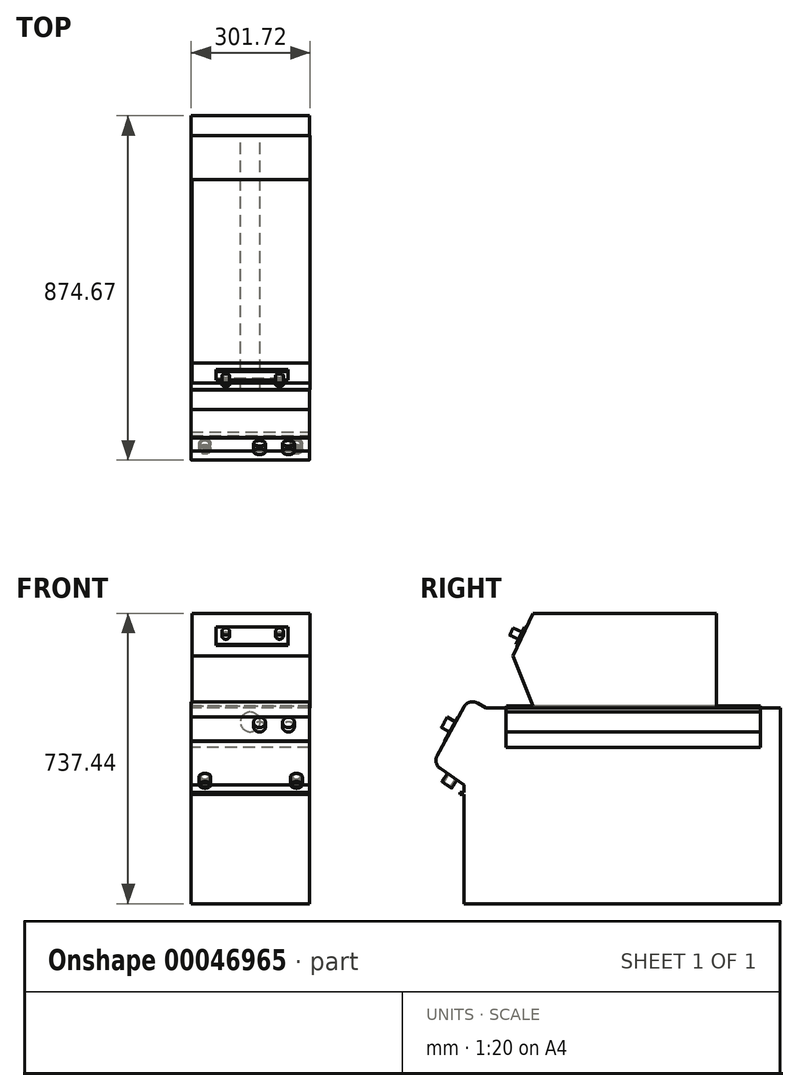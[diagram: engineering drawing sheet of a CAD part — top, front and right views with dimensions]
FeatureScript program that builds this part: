
annotation { "Feature Type Name" : "Feature", "Feature Type Description" : "" }
export const myFeature = defineFeature(function(context is Context, id is Id, definition is map)
    precondition{}
    {
        {
            var Q0;
            Q0=qCreatedBy(makeId("Right.planeOp"),FACE);
            var sketch = newSketch(context, id + "F0", { "sketchPlane" : qUnion([Q0])});
            skLineSegment(sketch, "E0.rect.top", {"start": v(-373.5, -248.5) * mm, "end": v(373.5, -248.5) * mm});
            skLineSegment(sketch, "E0.rect.left", {"start": v(-373.5, 248.5) * mm, "end": v(-373.5, -248.5) * mm});
            skLineSegment(sketch, "E0.rect.right", {"start": v(373.5, 248.5) * mm, "end": v(373.5, -248.5) * mm});
            skPoint(sketch, "E0.rect.middle", {"position": v(0, 0) * mm});
            skLineSegment(sketch, "E1", {"start": v(-323.5, 248.5) * mm, "end": v(-323.5, 148.5) * mm});
            skLineSegment(sketch, "E2", {"start": v(-323.5, 148.5) * mm, "end": v(323.5, 148.5) * mm});
            skLineSegment(sketch, "E3", {"start": v(323.5, 148.5) * mm, "end": v(323.5, 248.5) * mm});
            skLineSegment(sketch, "E4", {"start": v(-373.5, 248.5) * mm, "end": v(-323.5, 248.5) * mm});
            skLineSegment(sketch, "E5", {"start": v(323.5, 248.5) * mm, "end": v(373.5, 248.5) * mm});
            skSolve(sketch);
        }
        {
            var Q0;
            Q0=qSketchRegion(id+"F0",true);
            extrude(context, id + "F1", {"entities" : qUnion([Q0]), "depth" : 300 * mm});
        }
        {
            var Q0;
            Q0=makeQuery(id+"F1.opExtrude","SWEPT_FACE",FACE,{"disambiguationData":[OSD([sQuery(id+"F0.wireOp",EDGE,"E3")])]});
            var sketch = newSketch(context, id + "F2", { "sketchPlane" : qUnion([Q0])});
            skLineSegment(sketch, "E6", {"start": v(0, 248.5) * mm, "end": v(300, 148.5) * mm, "construction": true});
            skLineSegment(sketch, "E7", {"start": v(300, 248.5) * mm, "end": v(0, 148.5) * mm, "construction": true});
            skCircle(sketch, "E8", {"center": v(150, 213.5) * mm, "radius": 25 * mm});
            skPoint(sketch, "E8.centerSnap0", {"position": v(150, 198.5) * mm});
            skSolve(sketch);
        }
        {
            var Q0;
            Q0=qSketchRegion(id+"F2",true);
            var Q1;
            Q1=makeQuery(id+"F1.opExtrude","SWEPT_FACE",FACE,{"disambiguationData":[OSD([sQuery(id+"F0.wireOp",EDGE,"E1")])]});
            extrude(context, id + "F3", {"entities" : qUnion([Q0]), "endBound" : BoundingType.UP_TO_SURFACE, "endBoundEntityFace" : qUnion([Q1]), "depth" : 25 * mm});
        }
        {
            var Q0;
            Q0=makeQuery(id+"F1.opExtrude","CAP_FACE",FACE,{"disambiguationData":[OSD([sQuery(id+"F0.wireOp",EDGE,"E0.rect.top"),sQuery(id+"F0.wireOp",EDGE,"E0.rect.left"),sQuery(id+"F0.wireOp",EDGE,"E0.rect.right"),sQuery(id+"F0.wireOp",EDGE,"E1"),sQuery(id+"F0.wireOp",EDGE,"E2"),sQuery(id+"F0.wireOp",EDGE,"E3"),sQuery(id+"F0.wireOp",EDGE,"E4"),sQuery(id+"F0.wireOp",EDGE,"E5")])],"isStart":false});
            var sketch = newSketch(context, id + "F4", { "sketchPlane" : qUnion([Q0])});
            skLineSegment(sketch, "E9", {"start": v(-373.5, 248.5) * mm, "end": v(-417.97, 273.97) * mm});
            skLineSegment(sketch, "E10", {"start": v(-417.97, 273.97) * mm, "end": v(-509.02, 107.56) * mm});
            skLineSegment(sketch, "E11", {"start": v(-509.02, 107.56) * mm, "end": v(-429.45, 53.73) * mm});
            skLineSegment(sketch, "E12", {"start": v(-429.45, 53.73) * mm, "end": v(-429.45, -248.5) * mm});
            skLineSegment(sketch, "E13", {"start": v(-429.45, -248.5) * mm, "end": v(-373.5, -248.5) * mm});
            skSolve(sketch);
        }
        {
            var Q0;
            Q0=makeQuery(id+"F4.imprint","IMPRINT",FACE,{"disambiguationData":[TD([[makeQuery(id+"F4.imprint","IMPRINT",EDGE,{"derivedFrom":sQuery(id+"F4.wireOp",EDGE,"E9")}),1.0]])]});
            extrude(context, id + "F5", {"entities" : qUnion([Q0]), "operationType" : NewBodyOperationType.ADD, "oppositeDirection" : true, "depth" : 300 * mm});
        }
        {
            var Q0;
            Q0=makeQuery(id+"F5.opExtrude","SWEPT_EDGE",EDGE,{"disambiguationData":[OSD([sQuery(id+"F4.wireOp",EDGE,"E9"),sQuery(id+"F4.wireOp",EDGE,"E10")])]});
            fillet(context, id + "F6", {"entities" : qUnion([Q0]), "radius" : 25 * mm, "tangentPropagation" : true, "allowEdgeOverflow" : false});
        }
        {
            var Q0;
            Q0=makeQuery(id+"F5.opExtrude","SWEPT_EDGE",EDGE,{"disambiguationData":[OSD([sQuery(id+"F4.wireOp",EDGE,"E10"),sQuery(id+"F4.wireOp",EDGE,"E11")])]});
            fillet(context, id + "F7", {"entities" : qUnion([Q0]), "radius" : 25 * mm, "tangentPropagation" : true, "allowEdgeOverflow" : false});
        }
        {
            var Q0;
            Q0=makeQuery(id+"F5.opExtrude","SWEPT_FACE",FACE,{"disambiguationData":[OSD([sQuery(id+"F4.wireOp",EDGE,"E10")])]});
            var sketch = newSketch(context, id + "F8", { "sketchPlane" : qUnion([Q0])});
            skCircle(sketch, "E14", {"center": v(247, -44.1) * mm, "radius": 15 * mm});
            skCircle(sketch, "E15", {"center": v(173.6, -44.1) * mm, "radius": 15 * mm});
            skLineSegment(sketch, "E16.bottom", {"start": v(0, -15) * mm, "end": v(300, -15) * mm});
            skLineSegment(sketch, "E16.top", {"start": v(0, -85.4) * mm, "end": v(300, -85.4) * mm});
            skLineSegment(sketch, "E16.left", {"start": v(0, -15) * mm, "end": v(0, -85.4) * mm});
            skLineSegment(sketch, "E16.right", {"start": v(300, -15) * mm, "end": v(300, -85.4) * mm});
            skLineSegment(sketch, "E17", {"start": v(173.6, -44.1) * mm, "end": v(247, -44.1) * mm, "construction": true});
            skSolve(sketch);
        }
        {
            var Q0;
            Q0=makeQuery(id+"F8.imprint","IMPRINT",FACE,{"disambiguationData":[TD([[makeQuery(id+"F8.imprint","IMPRINT",EDGE,{"derivedFrom":sQuery(id+"F8.wireOp",EDGE,"E14")}),-1.0]])]});
            extrude(context, id + "F9", {"entities" : qUnion([Q0]), "depth" : 1 * mm});
        }
        {
            var Q0;
            Q0=makeQuery(id+"F8.imprint","IMPRINT",FACE,{"disambiguationData":[TD([[makeQuery(id+"F8.imprint","IMPRINT",EDGE,{"derivedFrom":sQuery(id+"F8.wireOp",EDGE,"E15")}),1.0]])]});
            extrude(context, id + "F10", {"entities" : qUnion([Q0]), "depth" : 25 * mm});
        }
        {
            var Q0;
            Q0=makeQuery(id+"F8.imprint","IMPRINT",FACE,{"disambiguationData":[TD([[makeQuery(id+"F8.imprint","IMPRINT",EDGE,{"derivedFrom":sQuery(id+"F8.wireOp",EDGE,"E14")}),1.0]])]});
            extrude(context, id + "F11", {"entities" : qUnion([Q0]), "depth" : 25 * mm});
        }
        {
            var Q0;
            Q0=makeQuery(id+"F5.opExtrude","SWEPT_FACE",FACE,{"disambiguationData":[OSD([sQuery(id+"F4.wireOp",EDGE,"E11")])]});
            var sketch = newSketch(context, id + "F12", { "sketchPlane" : qUnion([Q0])});
            skCircle(sketch, "E18", {"center": v(34.76, 422.44) * mm, "radius": 15 * mm});
            skPoint(sketch, "E18.centerSnap0", {"position": v(0, 422.44) * mm});
            skCircle(sketch, "E19", {"center": v(267.24, 422.44) * mm, "radius": 15 * mm});
            skCircle(sketch, "E20", {"center": v(34.76, 422.44) * mm, "radius": 10 * mm});
            skCircle(sketch, "E21", {"center": v(267.24, 422.44) * mm, "radius": 10 * mm});
            skSolve(sketch);
        }
        {
            var Q0;
            Q0=qSketchRegion(id+"F12",true);
            extrude(context, id + "F13", {"entities" : qUnion([Q0]), "depth" : 25 * mm});
        }
        {
            var Q0;
            Q0=makeQuery(id+"F5.opExtrude","SWEPT_FACE",FACE,{"disambiguationData":[OSD([sQuery(id+"F4.wireOp",EDGE,"E12")])]});
            var sketch = newSketch(context, id + "F14", { "sketchPlane" : qUnion([Q0])});
            skLineSegment(sketch, "E22.bottom", {"start": v(0, 41.73) * mm, "end": v(300, 41.73) * mm});
            skLineSegment(sketch, "E22.top", {"start": v(0, -238.27) * mm, "end": v(300, -238.27) * mm});
            skLineSegment(sketch, "E22.left", {"start": v(0, 41.73) * mm, "end": v(0, -238.27) * mm});
            skLineSegment(sketch, "E22.right", {"start": v(300, 41.73) * mm, "end": v(300, -238.27) * mm});
            skLineSegment(sketch, "E23.bottom", {"start": v(0, 34.33) * mm, "end": v(300, 34.33) * mm});
            skLineSegment(sketch, "E23.top", {"start": v(0, 29.42) * mm, "end": v(300, 29.42) * mm});
            skLineSegment(sketch, "E23.left", {"start": v(0, 34.33) * mm, "end": v(0, 29.42) * mm});
            skLineSegment(sketch, "E23.right", {"start": v(300, 34.33) * mm, "end": v(300, 29.42) * mm});
            skLineSegment(sketch, "E24", {"start": v(0, -97.39) * mm, "end": v(300, -97.39) * mm, "construction": true});
            skLineSegment(sketch, "E25.MirrorCS", {"start": v(300, -229.1) * mm, "end": v(300, -224.2) * mm});
            skLineSegment(sketch, "E26.MirrorCS", {"start": v(0, -229.1) * mm, "end": v(0, -224.2) * mm});
            skLineSegment(sketch, "E27.MirrorCS", {"start": v(0, -229.1) * mm, "end": v(300, -229.1) * mm});
            skLineSegment(sketch, "E28.MirrorCS", {"start": v(0, -224.2) * mm, "end": v(300, -224.2) * mm});
            skLineSegment(sketch, "E29", {"start": v(0, 24.35) * mm, "end": v(300, 24.35) * mm, "construction": true});
            skLineSegment(sketch, "E30.MirrorCS", {"start": v(0, 14.36) * mm, "end": v(0, 19.27) * mm});
            skLineSegment(sketch, "E31.MirrorCS", {"start": v(300, 14.36) * mm, "end": v(300, 19.27) * mm});
            skLineSegment(sketch, "E32.MirrorCS", {"start": v(0, 14.36) * mm, "end": v(300, 14.36) * mm});
            skLineSegment(sketch, "E33.MirrorCS", {"start": v(0, 19.27) * mm, "end": v(300, 19.27) * mm});
            skLineSegment(sketch, "E34.MirrorCS", {"start": v(0, 6.97) * mm, "end": v(300, 6.97) * mm, "construction": true});
            skLineSegment(sketch, "E35.MirrorCS", {"start": v(0, -20.4) * mm, "end": v(0, -15.49) * mm});
            skLineSegment(sketch, "E36.MirrorCS", {"start": v(300, -20.4) * mm, "end": v(300, -15.49) * mm});
            skLineSegment(sketch, "E37.MirrorCS", {"start": v(0, -0.43) * mm, "end": v(0, -5.34) * mm});
            skLineSegment(sketch, "E38.MirrorCS", {"start": v(300, -0.43) * mm, "end": v(300, -5.34) * mm});
            skLineSegment(sketch, "E39.MirrorCS", {"start": v(0, -20.4) * mm, "end": v(300, -20.4) * mm});
            skLineSegment(sketch, "E40.MirrorCS", {"start": v(0, -15.49) * mm, "end": v(300, -15.49) * mm});
            skLineSegment(sketch, "E41.MirrorCS", {"start": v(0, -27.8) * mm, "end": v(300, -27.8) * mm, "construction": true});
            skLineSegment(sketch, "E42.MirrorCS", {"start": v(0, -5.34) * mm, "end": v(300, -5.34) * mm});
            skLineSegment(sketch, "E43.MirrorCS", {"start": v(0, -0.43) * mm, "end": v(300, -0.43) * mm});
            skLineSegment(sketch, "E44.MirrorCS", {"start": v(0, -10.41) * mm, "end": v(300, -10.41) * mm, "construction": true});
            skLineSegment(sketch, "E45.MirrorCS", {"start": v(300, -89.92) * mm, "end": v(300, -85) * mm});
            skLineSegment(sketch, "E46.MirrorCS", {"start": v(300, -35.2) * mm, "end": v(300, -40.1) * mm});
            skLineSegment(sketch, "E47.MirrorCS", {"start": v(0, -35.2) * mm, "end": v(0, -40.1) * mm});
            skLineSegment(sketch, "E48.MirrorCS", {"start": v(300, -69.95) * mm, "end": v(300, -74.86) * mm});
            skLineSegment(sketch, "E49.MirrorCS", {"start": v(0, -69.95) * mm, "end": v(0, -74.86) * mm});
            skLineSegment(sketch, "E50.MirrorCS", {"start": v(300, -55.16) * mm, "end": v(300, -50.25) * mm});
            skLineSegment(sketch, "E51.MirrorCS", {"start": v(0, -55.16) * mm, "end": v(0, -50.25) * mm});
            skLineSegment(sketch, "E52.MirrorCS", {"start": v(0, -89.92) * mm, "end": v(0, -85) * mm});
            skLineSegment(sketch, "E53.MirrorCS", {"start": v(0, -55.16) * mm, "end": v(300, -55.16) * mm});
            skLineSegment(sketch, "E54.MirrorCS", {"start": v(0, -69.95) * mm, "end": v(300, -69.95) * mm});
            skLineSegment(sketch, "E55.MirrorCS", {"start": v(0, -50.25) * mm, "end": v(300, -50.25) * mm});
            skLineSegment(sketch, "E56.MirrorCS", {"start": v(0, -97.31) * mm, "end": v(300, -97.31) * mm, "construction": true});
            skLineSegment(sketch, "E57.MirrorCS", {"start": v(0, -79.93) * mm, "end": v(300, -79.93) * mm, "construction": true});
            skLineSegment(sketch, "E58.MirrorCS", {"start": v(0, -62.55) * mm, "end": v(300, -62.55) * mm, "construction": true});
            skLineSegment(sketch, "E59.MirrorCS", {"start": v(0, -89.92) * mm, "end": v(300, -89.92) * mm});
            skLineSegment(sketch, "E60.MirrorCS", {"start": v(0, -40.1) * mm, "end": v(300, -40.1) * mm});
            skLineSegment(sketch, "E61.MirrorCS", {"start": v(0, -45.17) * mm, "end": v(300, -45.17) * mm, "construction": true});
            skLineSegment(sketch, "E62.MirrorCS", {"start": v(0, -74.86) * mm, "end": v(300, -74.86) * mm});
            skLineSegment(sketch, "E63.MirrorCS", {"start": v(0, -35.2) * mm, "end": v(300, -35.2) * mm});
            skLineSegment(sketch, "E64.MirrorCS", {"start": v(0, -85) * mm, "end": v(300, -85) * mm});
            skLineSegment(sketch, "E65.MirrorCS", {"start": v(300, -174.38) * mm, "end": v(300, -179.29) * mm});
            skLineSegment(sketch, "E66.MirrorCS", {"start": v(0, -139.62) * mm, "end": v(0, -144.53) * mm});
            skLineSegment(sketch, "E67.MirrorCS", {"start": v(0, -174.38) * mm, "end": v(0, -179.29) * mm});
            skLineSegment(sketch, "E68.MirrorCS", {"start": v(0, -124.82) * mm, "end": v(0, -119.91) * mm});
            skLineSegment(sketch, "E69.MirrorCS", {"start": v(0, -194.34) * mm, "end": v(0, -189.43) * mm});
            skLineSegment(sketch, "E70.MirrorCS", {"start": v(300, -139.62) * mm, "end": v(300, -144.53) * mm});
            skLineSegment(sketch, "E71.MirrorCS", {"start": v(300, -124.82) * mm, "end": v(300, -119.91) * mm});
            skLineSegment(sketch, "E72.MirrorCS", {"start": v(300, -104.86) * mm, "end": v(300, -109.77) * mm});
            skLineSegment(sketch, "E73.MirrorCS", {"start": v(0, -104.86) * mm, "end": v(0, -109.77) * mm});
            skLineSegment(sketch, "E74.MirrorCS", {"start": v(300, -209.14) * mm, "end": v(300, -214.05) * mm});
            skLineSegment(sketch, "E75.MirrorCS", {"start": v(300, -194.34) * mm, "end": v(300, -189.43) * mm});
            skLineSegment(sketch, "E76.MirrorCS", {"start": v(0, -159.58) * mm, "end": v(0, -154.67) * mm});
            skLineSegment(sketch, "E77.MirrorCS", {"start": v(0, -209.14) * mm, "end": v(0, -214.05) * mm});
            skLineSegment(sketch, "E78.MirrorCS", {"start": v(300, -159.58) * mm, "end": v(300, -154.67) * mm});
            skLineSegment(sketch, "E79.MirrorCS", {"start": v(0, -194.34) * mm, "end": v(300, -194.34) * mm});
            skLineSegment(sketch, "E80.MirrorCS", {"start": v(0, -104.86) * mm, "end": v(300, -104.86) * mm});
            skLineSegment(sketch, "E81.MirrorCS", {"start": v(0, -109.77) * mm, "end": v(300, -109.77) * mm});
            skLineSegment(sketch, "E82.MirrorCS", {"start": v(0, -209.14) * mm, "end": v(300, -209.14) * mm});
            skLineSegment(sketch, "E83.MirrorCS", {"start": v(0, -149.6) * mm, "end": v(300, -149.6) * mm, "construction": true});
            skLineSegment(sketch, "E84.MirrorCS", {"start": v(0, -189.43) * mm, "end": v(300, -189.43) * mm});
            skLineSegment(sketch, "E85.MirrorCS", {"start": v(0, -132.22) * mm, "end": v(300, -132.22) * mm, "construction": true});
            skLineSegment(sketch, "E86.MirrorCS", {"start": v(0, -144.53) * mm, "end": v(300, -144.53) * mm});
            skLineSegment(sketch, "E87.MirrorCS", {"start": v(0, -174.38) * mm, "end": v(300, -174.38) * mm});
            skLineSegment(sketch, "E88.MirrorCS", {"start": v(0, -214.05) * mm, "end": v(300, -214.05) * mm});
            skLineSegment(sketch, "E89.MirrorCS", {"start": v(0, -154.67) * mm, "end": v(300, -154.67) * mm});
            skLineSegment(sketch, "E90.MirrorCS", {"start": v(0, -184.36) * mm, "end": v(300, -184.36) * mm, "construction": true});
            skLineSegment(sketch, "E91.MirrorCS", {"start": v(0, -166.98) * mm, "end": v(300, -166.98) * mm, "construction": true});
            skLineSegment(sketch, "E92.MirrorCS", {"start": v(0, -114.84) * mm, "end": v(300, -114.84) * mm, "construction": true});
            skLineSegment(sketch, "E93.MirrorCS", {"start": v(0, -236.5) * mm, "end": v(300, -236.5) * mm});
            skLineSegment(sketch, "E94.MirrorCS", {"start": v(0, -119.91) * mm, "end": v(300, -119.91) * mm});
            skLineSegment(sketch, "E95.MirrorCS", {"start": v(0, -139.62) * mm, "end": v(300, -139.62) * mm});
            skLineSegment(sketch, "E96.MirrorCS", {"start": v(0, -219.12) * mm, "end": v(300, -219.12) * mm, "construction": true});
            skLineSegment(sketch, "E97.MirrorCS", {"start": v(0, -124.82) * mm, "end": v(300, -124.82) * mm});
            skLineSegment(sketch, "E98.MirrorCS", {"start": v(0, -159.58) * mm, "end": v(300, -159.58) * mm});
            skLineSegment(sketch, "E99.MirrorCS", {"start": v(0, -97.46) * mm, "end": v(300, -97.46) * mm, "construction": true});
            skLineSegment(sketch, "E100.MirrorCS", {"start": v(0, -179.29) * mm, "end": v(300, -179.29) * mm});
            skLineSegment(sketch, "E101.MirrorCS", {"start": v(0, -201.74) * mm, "end": v(300, -201.74) * mm, "construction": true});
            skSolve(sketch);
        }
        {
            var Q0;
            Q0=makeQuery(id+"F14.imprint","IMPRINT",FACE,{"disambiguationData":[TD([[makeQuery(id+"F14.imprint","IMPRINT",EDGE,{"derivedFrom":sQuery(id+"F14.wireOp",EDGE,"E23.bottom")}),-1.0]])]});
            var Q1;
            Q1=makeQuery(id+"F14.imprint","IMPRINT",FACE,{"disambiguationData":[TD([[makeQuery(id+"F14.imprint","IMPRINT",EDGE,{"derivedFrom":sQuery(id+"F14.wireOp",EDGE,"E30.MirrorCS")}),1.0]])]});
            var Q2;
            Q2=makeQuery(id+"F14.imprint","IMPRINT",FACE,{"disambiguationData":[TD([[makeQuery(id+"F14.imprint","IMPRINT",EDGE,{"derivedFrom":sQuery(id+"F14.wireOp",EDGE,"E37.MirrorCS")}),1.0]])]});
            var Q3;
            Q3=makeQuery(id+"F14.imprint","IMPRINT",FACE,{"disambiguationData":[TD([[makeQuery(id+"F14.imprint","IMPRINT",EDGE,{"derivedFrom":sQuery(id+"F14.wireOp",EDGE,"E35.MirrorCS")}),1.0]])]});
            var Q4;
            Q4=makeQuery(id+"F14.imprint","IMPRINT",FACE,{"disambiguationData":[TD([[makeQuery(id+"F14.imprint","IMPRINT",EDGE,{"derivedFrom":sQuery(id+"F14.wireOp",EDGE,"E46.MirrorCS")}),-1.0]])]});
            var Q5;
            Q5=makeQuery(id+"F14.imprint","IMPRINT",FACE,{"disambiguationData":[TD([[makeQuery(id+"F14.imprint","IMPRINT",EDGE,{"derivedFrom":sQuery(id+"F14.wireOp",EDGE,"E50.MirrorCS")}),-1.0]])]});
            var Q6;
            Q6=makeQuery(id+"F14.imprint","IMPRINT",FACE,{"disambiguationData":[TD([[makeQuery(id+"F14.imprint","IMPRINT",EDGE,{"derivedFrom":sQuery(id+"F14.wireOp",EDGE,"E48.MirrorCS")}),-1.0]])]});
            var Q7;
            Q7=makeQuery(id+"F14.imprint","IMPRINT",FACE,{"disambiguationData":[TD([[makeQuery(id+"F14.imprint","IMPRINT",EDGE,{"derivedFrom":sQuery(id+"F14.wireOp",EDGE,"E45.MirrorCS")}),-1.0]])]});
            var Q8;
            Q8=makeQuery(id+"F14.imprint","IMPRINT",FACE,{"disambiguationData":[TD([[makeQuery(id+"F14.imprint","IMPRINT",EDGE,{"derivedFrom":sQuery(id+"F14.wireOp",EDGE,"E72.MirrorCS")}),-1.0]])]});
            var Q9;
            Q9=makeQuery(id+"F14.imprint","IMPRINT",FACE,{"disambiguationData":[TD([[makeQuery(id+"F14.imprint","IMPRINT",EDGE,{"derivedFrom":sQuery(id+"F14.wireOp",EDGE,"E68.MirrorCS")}),1.0]])]});
            var Q10;
            Q10=makeQuery(id+"F14.imprint","IMPRINT",FACE,{"disambiguationData":[TD([[makeQuery(id+"F14.imprint","IMPRINT",EDGE,{"derivedFrom":sQuery(id+"F14.wireOp",EDGE,"E66.MirrorCS")}),1.0]])]});
            var Q11;
            Q11=makeQuery(id+"F14.imprint","IMPRINT",FACE,{"disambiguationData":[TD([[makeQuery(id+"F14.imprint","IMPRINT",EDGE,{"derivedFrom":sQuery(id+"F14.wireOp",EDGE,"E76.MirrorCS")}),1.0]])]});
            var Q12;
            Q12=makeQuery(id+"F14.imprint","IMPRINT",FACE,{"disambiguationData":[TD([[makeQuery(id+"F14.imprint","IMPRINT",EDGE,{"derivedFrom":sQuery(id+"F14.wireOp",EDGE,"E65.MirrorCS")}),-1.0]])]});
            var Q13;
            Q13=makeQuery(id+"F14.imprint","IMPRINT",FACE,{"disambiguationData":[TD([[makeQuery(id+"F14.imprint","IMPRINT",EDGE,{"derivedFrom":sQuery(id+"F14.wireOp",EDGE,"E69.MirrorCS")}),1.0]])]});
            var Q14;
            Q14=makeQuery(id+"F14.imprint","IMPRINT",FACE,{"disambiguationData":[TD([[makeQuery(id+"F14.imprint","IMPRINT",EDGE,{"derivedFrom":sQuery(id+"F14.wireOp",EDGE,"E74.MirrorCS")}),-1.0]])]});
            var Q15;
            Q15=makeQuery(id+"F14.imprint","IMPRINT",FACE,{"disambiguationData":[TD([[makeQuery(id+"F14.imprint","IMPRINT",EDGE,{"derivedFrom":sQuery(id+"F14.wireOp",EDGE,"E26.MirrorCS")}),1.0]])]});
            extrude(context, id + "F15", {"entities" : qUnion([Q0, Q1, Q2, Q3, Q4, Q5, Q6, Q7, Q8, Q9, Q10, Q11, Q12, Q13, Q14, Q15]), "operationType" : NewBodyOperationType.ADD, "depth" : 10 * mm});
        }
        {
            var Q0;
            Q0=makeQuery(id+"F1.opExtrude","SWEPT_FACE",FACE,{"disambiguationData":[OSD([sQuery(id+"F0.wireOp",EDGE,"E5")])]});
            var sketch = newSketch(context, id + "F16", { "sketchPlane" : qUnion([Q0])});
            skLineSegment(sketch, "E102.bottom", {"start": v(0, 323.5) * mm, "end": v(301.72, 323.5) * mm});
            skLineSegment(sketch, "E102.top", {"start": v(0, -322.28) * mm, "end": v(301.72, -322.28) * mm});
            skLineSegment(sketch, "E102.left", {"start": v(0, 323.5) * mm, "end": v(0, -322.28) * mm});
            skLineSegment(sketch, "E102.right", {"start": v(301.72, 323.5) * mm, "end": v(301.72, -322.28) * mm});
            skSolve(sketch);
        }
        {
            var Q0;
            Q0=makeQuery(id+"F16.imprint","IMPRINT",FACE,{"disambiguationData":[TD([[makeQuery(id+"F16.imprint","IMPRINT",EDGE,{"derivedFrom":sQuery(id+"F16.wireOp",EDGE,"E102.top")}),1.0]])]});
            extrude(context, id + "F17", {"entities" : qUnion([Q0]), "depth" : 5 * mm});
        }
        {
            var Q0;
            Q0=makeQuery(id+"F17.opExtrude","SWEPT_FACE",FACE,{"disambiguationData":[OSD([sQuery(id+"F16.wireOp",EDGE,"E102.right")])]});
            var sketch = newSketch(context, id + "F18", { "sketchPlane" : qUnion([Q0])});
            skLineSegment(sketch, "E103", {"start": v(-255.04, 253.5) * mm, "end": v(-255.04, 488.94) * mm});
            skLineSegment(sketch, "E104", {"start": v(-255.04, 488.94) * mm, "end": v(211.7, 488.94) * mm});
            skLineSegment(sketch, "E105", {"start": v(211.7, 488.94) * mm, "end": v(211.7, 253.5) * mm});
            skLineSegment(sketch, "E106", {"start": v(211.7, 253.5) * mm, "end": v(-255.04, 253.5) * mm});
            skSolve(sketch);
        }
        {
            var Q0;
            Q0=makeQuery(id+"F18.imprint","IMPRINT",FACE,{"disambiguationData":[TD([[makeQuery(id+"F18.imprint","IMPRINT",EDGE,{"derivedFrom":sQuery(id+"F18.wireOp",EDGE,"E103")}),-1.0]])]});
            extrude(context, id + "F19", {"entities" : qUnion([Q0]), "operationType" : NewBodyOperationType.ADD, "oppositeDirection" : true, "depth" : 300 * mm});
        }
        {
            var Q0;
            Q0=makeQuery(id+"F19.boolean.opBoolean","MERGE",FACE,{"derivedFrom":[makeQuery(id+"F17.opExtrude","SWEPT_FACE",FACE,{"disambiguationData":[OSD([sQuery(id+"F16.wireOp",EDGE,"E102.right")])]}),makeQuery(id+"F19.opExtrude","CAP_FACE",FACE,{"disambiguationData":[OSD([sQuery(id+"F18.wireOp",EDGE,"E103"),sQuery(id+"F18.wireOp",EDGE,"E104"),sQuery(id+"F18.wireOp",EDGE,"E105"),sQuery(id+"F18.wireOp",EDGE,"E106")])],"isStart":true})]});
            var sketch = newSketch(context, id + "F20", { "sketchPlane" : qUnion([Q0])});
            skLineSegment(sketch, "E107", {"start": v(-255.04, 253.5) * mm, "end": v(-305.13, 381.53) * mm});
            skLineSegment(sketch, "E108", {"start": v(-305.13, 381.53) * mm, "end": v(-255.04, 488.94) * mm});
            skSolve(sketch);
        }
        {
            var Q0;
            Q0=qSketchRegion(id+"F20",true);
            var Q1;
            Q1=makeQuery(id+"F20.imprint","IMPRINT",FACE,{"disambiguationData":[TD([[makeQuery(id+"F20.imprint","IMPRINT",EDGE,{"derivedFrom":sQuery(id+"F20.wireOp",EDGE,"E107")}),-1.0]])]});
            extrude(context, id + "F21", {"entities" : qUnion([Q0, Q1]), "operationType" : NewBodyOperationType.ADD, "oppositeDirection" : true, "depth" : 300 * mm});
        }
        {
            var Q0;
            Q0=makeQuery(id+"F21.opExtrude","SWEPT_FACE",FACE,{"disambiguationData":[OSD([sQuery(id+"F20.wireOp",EDGE,"E108")])]});
            var sketch = newSketch(context, id + "F22", { "sketchPlane" : qUnion([Q0])});
            skLineSegment(sketch, "E109.bottom", {"start": v(62.72, 295.84) * mm, "end": v(245.33, 295.84) * mm});
            skLineSegment(sketch, "E109.top", {"start": v(62.72, 245.64) * mm, "end": v(245.33, 245.64) * mm});
            skLineSegment(sketch, "E109.left", {"start": v(62.72, 295.84) * mm, "end": v(62.72, 245.64) * mm});
            skLineSegment(sketch, "E109.right", {"start": v(245.33, 295.84) * mm, "end": v(245.33, 245.64) * mm});
            skSolve(sketch);
        }
        {
            var Q0;
            Q0=makeQuery(id+"F22.imprint","IMPRINT",FACE,{"disambiguationData":[TD([[makeQuery(id+"F22.imprint","IMPRINT",EDGE,{"derivedFrom":sQuery(id+"F22.wireOp",EDGE,"E109.bottom")}),-1.0]])]});
            extrude(context, id + "F23", {"entities" : qUnion([Q0]), "depth" : 5 * mm});
        }
        {
            var Q0;
            Q0=makeQuery(id+"F23.opExtrude","CAP_FACE",FACE,{"disambiguationData":[OSD([sQuery(id+"F22.wireOp",EDGE,"E109.bottom"),sQuery(id+"F22.wireOp",EDGE,"E109.top"),sQuery(id+"F22.wireOp",EDGE,"E109.left"),sQuery(id+"F22.wireOp",EDGE,"E109.right")])],"isStart":false});
            var sketch = newSketch(context, id + "F24", { "sketchPlane" : qUnion([Q0])});
            skCircle(sketch, "E110", {"center": v(87.88, 270.74) * mm, "radius": 10 * mm});
            skPoint(sketch, "E110.centerSnap0", {"position": v(62.72, 270.74) * mm});
            skCircle(sketch, "E111", {"center": v(224.2, 270.74) * mm, "radius": 10 * mm});
            skSolve(sketch);
        }
        {
            var Q0;
            Q0=qSketchRegion(id+"F24",true);
            extrude(context, id + "F25", {"entities" : qUnion([Q0]), "depth" : 25 * mm});
        }
    });
